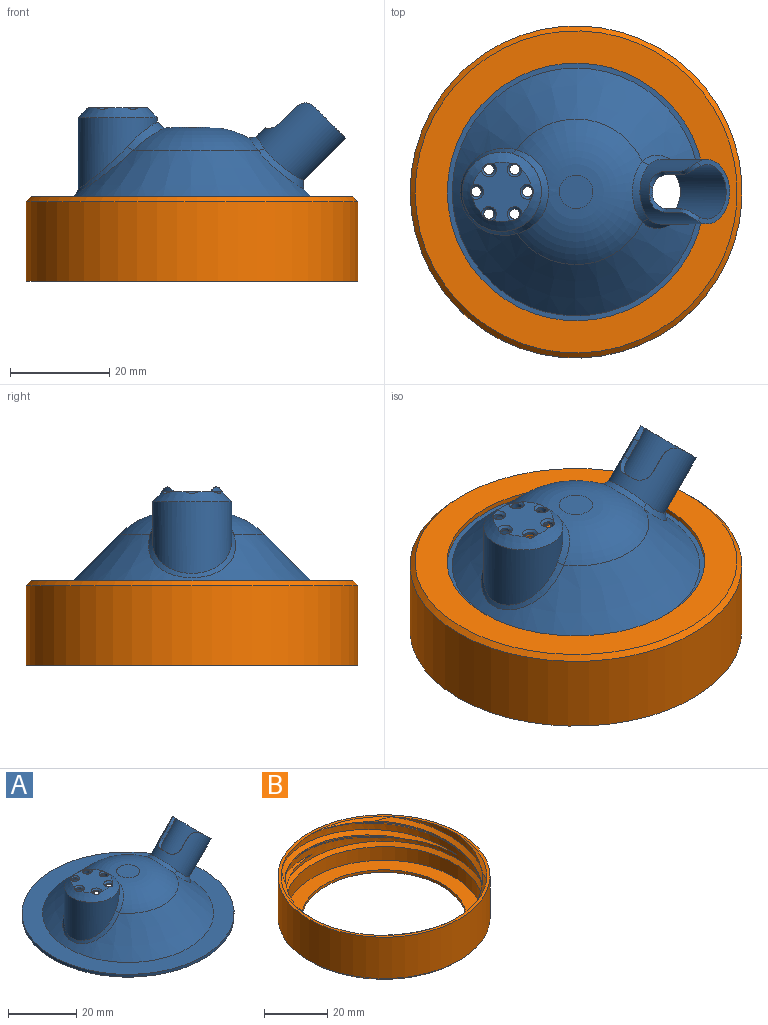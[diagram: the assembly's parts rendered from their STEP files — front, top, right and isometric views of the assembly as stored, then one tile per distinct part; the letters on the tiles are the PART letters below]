
ASSEMBLY  parts=2 mates=1
PART A: 45 faces, bbox 62x62x23 mm
  f0: plane 12x11.69mm, normal (0,0,1), area 78.9mm2, adj f1,f34,f36,f38,f40,f42,f44
  f1: cone r=6mm half-angle=45deg, axis (0,0,-1), area 119mm2, adj f0,f10,f34,f36,f38,f40,f42,f44
  f2: cone r=5.29mm half-angle=45deg, axis (0,0,-1), area 71.2mm2, adj f14,f15,f33,f35,f37,f39,f41,f43
  f3: cylinder r=6.5mm len=18.56mm, axis (0.71,0,0.71), area 434.9mm2, adj f9,f16,f17,f18,f19,f20,f21,f22
  f4: cone r=25mm half-angle=45deg, axis (0,0,-1), area 1484.6mm2, adj f7,f24,f29,f31
  f5: plane 62x62mm, normal (0,0,-1), area 1120.1mm2, adj f8,f11
  f6: plane 6.75x6.75mm, normal (0,0,1), area 35.7mm2, adj f24
  f7: plane 62x62mm, normal (0,0,1), area 1055.6mm2, adj f4,f8
  f8: cylinder r=31mm len=62mm, axis (0,0,1), area 194.8mm2, adj f5,f7
  f9: plane 13x6.43mm, normal (0.71,0,0.71), area 23.2mm2, adj f3,f13,f19,f20
  f10: cylinder r=8mm len=16mm, axis (0,0,-1), area 343.7mm2, adj f1,f31,f32
  f11: cone r=24.29mm half-angle=45deg, axis (0,0,-1), area 1516.3mm2, adj f5,f23,f25,f27
  f12: plane 5.92x5.92mm, normal (0,0,-1), area 27.5mm2, adj f23
  f13: cylinder r=5.5mm len=17.69mm, axis (0.71,0,0.71), area 397.9mm2, adj f9,f16,f17,f18,f19,f20,f21,f22
  f14: cylinder r=7mm len=14.48mm, axis (0,0,-1), area 326.3mm2, adj f2,f27,f28
  f15: plane 11.17x11mm, normal (0,0,-1), area 83.8mm2, adj f2,f33,f35,f37,f39,f41,f43
  f16: plane 3.38x3.38mm, normal (-0.44,0.78,0.44), area 4mm2, adj f3,f13,f19,f21
  f17: plane 3.38x3.38mm, normal (-0.44,-0.78,0.44), area 4mm2, adj f3,f13,f20,f22
  f18: plane 2.6x0.73mm, normal (0.71,0,0.71), area 1.9mm2, adj f3,f13,f21,f22
  f19: cylinder r=3mm len=4.5mm, axis (-0.55,-0.63,0.55), area 5.1mm2, adj f3,f9,f13,f16
  f20: cylinder r=3mm len=4.5mm, axis (0.55,-0.63,-0.55), area 5.1mm2, adj f3,f9,f13,f17
  f21: cylinder r=3mm len=4.5mm, axis (0.55,0.63,-0.55), area 5.1mm2, adj f3,f13,f16,f18
  f22: cylinder r=3mm len=4.5mm, axis (-0.55,0.63,0.55), area 5.1mm2, adj f3,f13,f17,f18
  f23: torus R=2.96mm, axis (0,0,-1), area 576.4mm2, adj f11,f12,f26,f28
  f24: torus R=3.37mm, axis (0,0,-1), area 569.8mm2, adj f4,f6,f30,f32
  f25: bspline ~12.87x7.79mm, area 40.7mm2, adj f11,f13,f26
  f26: bspline ~10.65x3.04mm, area 17.8mm2, adj f13,f23,f25
  f27: bspline ~15.8x10.23mm, area 39.4mm2, adj f11,f14,f28
  f28: bspline ~15.02x6.73mm, area 40.2mm2, adj f14,f23,f27
  f29: bspline ~14.76x9.11mm, area 48.9mm2, adj f3,f4,f30
  f30: bspline ~12.2x3.28mm, area 20.7mm2, adj f3,f24,f29
  f31: bspline ~17.74x11.36mm, area 43mm2, adj f4,f10,f32
  f32: bspline ~16.91x7.45mm, area 44.1mm2, adj f10,f24,f31
  f33: cylinder r=1.03mm len=2.05mm, axis (0,0,1), area 4.5mm2, adj f2,f15,f34
  f34: cone r=1.03mm half-angle=45deg, axis (0,0,1), area 4.3mm2, adj f0,f1,f33
  f35: cylinder r=1.03mm len=2.05mm, axis (0,0,1), area 4.5mm2, adj f2,f15,f36
  f36: cone r=1.03mm half-angle=45deg, axis (0,0,1), area 4.3mm2, adj f0,f1,f35
  f37: cylinder r=1.03mm len=2.05mm, axis (0,0,1), area 4.5mm2, adj f2,f15,f38
  f38: cone r=1.03mm half-angle=45deg, axis (0,0,1), area 4.3mm2, adj f0,f1,f37
  f39: cylinder r=1.03mm len=2.05mm, axis (0,0,1), area 4.2mm2, adj f2,f15,f40
  f40: cone r=1.03mm half-angle=45deg, axis (0,0,1), area 4.3mm2, adj f0,f1,f39
  f41: cylinder r=1.03mm len=2.05mm, axis (0,0,1), area 4.2mm2, adj f2,f15,f42
  f42: cone r=1.03mm half-angle=45deg, axis (0,0,1), area 4.3mm2, adj f0,f1,f41
  f43: cylinder r=1.03mm len=2.05mm, axis (0,0,1), area 4.5mm2, adj f2,f15,f44
  f44: cone r=1.03mm half-angle=45deg, axis (0,0,1), area 4.3mm2, adj f0,f1,f43
PART B: 31 faces, bbox 68.3x68.3x18.3 mm
  f0: cylinder r=26mm len=52mm, axis (0,0,-1), area 163.4mm2, adj f1,f5
  f1: plane 62.5x62.5mm, normal (0,0,1), area 944.2mm2, adj f0,f2
  f2: cylinder r=31.25mm len=62.5mm, axis (0,0,-1), area 1030.8mm2, adj f1,f3
  f3: cone r=32.5mm half-angle=45deg, axis (0,0,1), area 354mm2, adj f2,f18
  f4: cylinder r=33.5mm len=67mm, axis (0,0,-1), area 3367.8mm2, adj f21,f30
  f5: plane 65x65mm, normal (0,0,-1), area 1194.6mm2, adj f0,f30
  f6: cylinder r=31.25mm len=52.9mm, axis (0,0,-1), area 29.9mm2, adj f7,f8,f28,f29
  f7: bspline ~58.79x34.17mm, area 117.5mm2, adj f6,f18,f28,f29
  f8: bspline ~58.79x53.28mm, area 117.6mm2, adj f6,f18,f28,f29
  f9: cylinder r=31.25mm len=52.9mm, axis (0,0,-1), area 29.9mm2, adj f10,f11,f26,f27
  f10: bspline ~58.79x34.17mm, area 117.5mm2, adj f9,f18,f19,f26,f27
  f11: bspline ~58.79x53.28mm, area 117.6mm2, adj f9,f18,f20,f26,f27
  f12: cylinder r=31.25mm len=52.9mm, axis (0,0,-1), area 29.9mm2, adj f13,f14,f24,f25
  f13: bspline ~58.79x34.17mm, area 117.5mm2, adj f12,f18,f24,f25
  f14: bspline ~58.79x53.28mm, area 117.6mm2, adj f12,f19,f24,f25
  f15: cylinder r=31.25mm len=52.9mm, axis (0,0,-1), area 29.9mm2, adj f16,f17,f22,f23
  f16: bspline ~58.79x34.17mm, area 117.5mm2, adj f15,f18,f22,f23
  f17: bspline ~58.79x53.28mm, area 117.6mm2, adj f15,f18,f22,f23
  f18: cylinder r=32.5mm len=65mm, axis (0,0,-1), area 862.3mm2, adj f3,f7,f8,f10,f11,f13,f16,f17
  f19: cylinder r=32.5mm len=53.75mm, axis (0,0,-1), area 156.5mm2, adj f10,f14,f18,f21
  f20: cylinder r=32.5mm len=21.25mm, axis (0,0,-1), area 29mm2, adj f11,f18,f21
  f21: plane 67x67mm, normal (0,0,1), area 207.3mm2, adj f4,f18,f19,f20,f22,f24,f26,f28
  f22: cone r=32.5mm half-angle=60deg, axis (0,0,1), area 23.2mm2, adj f15,f16,f17,f21
  f23: cone r=32.5mm half-angle=60deg, axis (0,0,-1), area 23.2mm2, adj f15,f16,f17,f18
  f24: cone r=32.5mm half-angle=60deg, axis (0,0,1), area 23.2mm2, adj f12,f13,f14,f21
  f25: cone r=32.5mm half-angle=60deg, axis (0,0,-1), area 23.2mm2, adj f12,f13,f14,f18
  f26: cone r=32.5mm half-angle=60deg, axis (0,0,1), area 23.2mm2, adj f9,f10,f11,f21
  f27: cone r=32.5mm half-angle=60deg, axis (0,0,-1), area 23.2mm2, adj f9,f10,f11,f18
  f28: cone r=32.5mm half-angle=60deg, axis (0,0,1), area 23.2mm2, adj f6,f7,f8,f21
  f29: cone r=32.5mm half-angle=60deg, axis (0,0,-1), area 23.2mm2, adj f6,f7,f8,f18
  f30: cone r=32.5mm half-angle=45deg, axis (0,0,1), area 293.2mm2, adj f4,f5
PLACE A t=(-16.44,4.3,5.97)mm fixed
PLACE B rot(axis=(1,0,0),180deg) t=(-16.44,4.3,7.97)mm
MATE fastened B.f0 <-> A.f4  axis (0,0,-1) through (-16.44,4.3,6.97)mm
